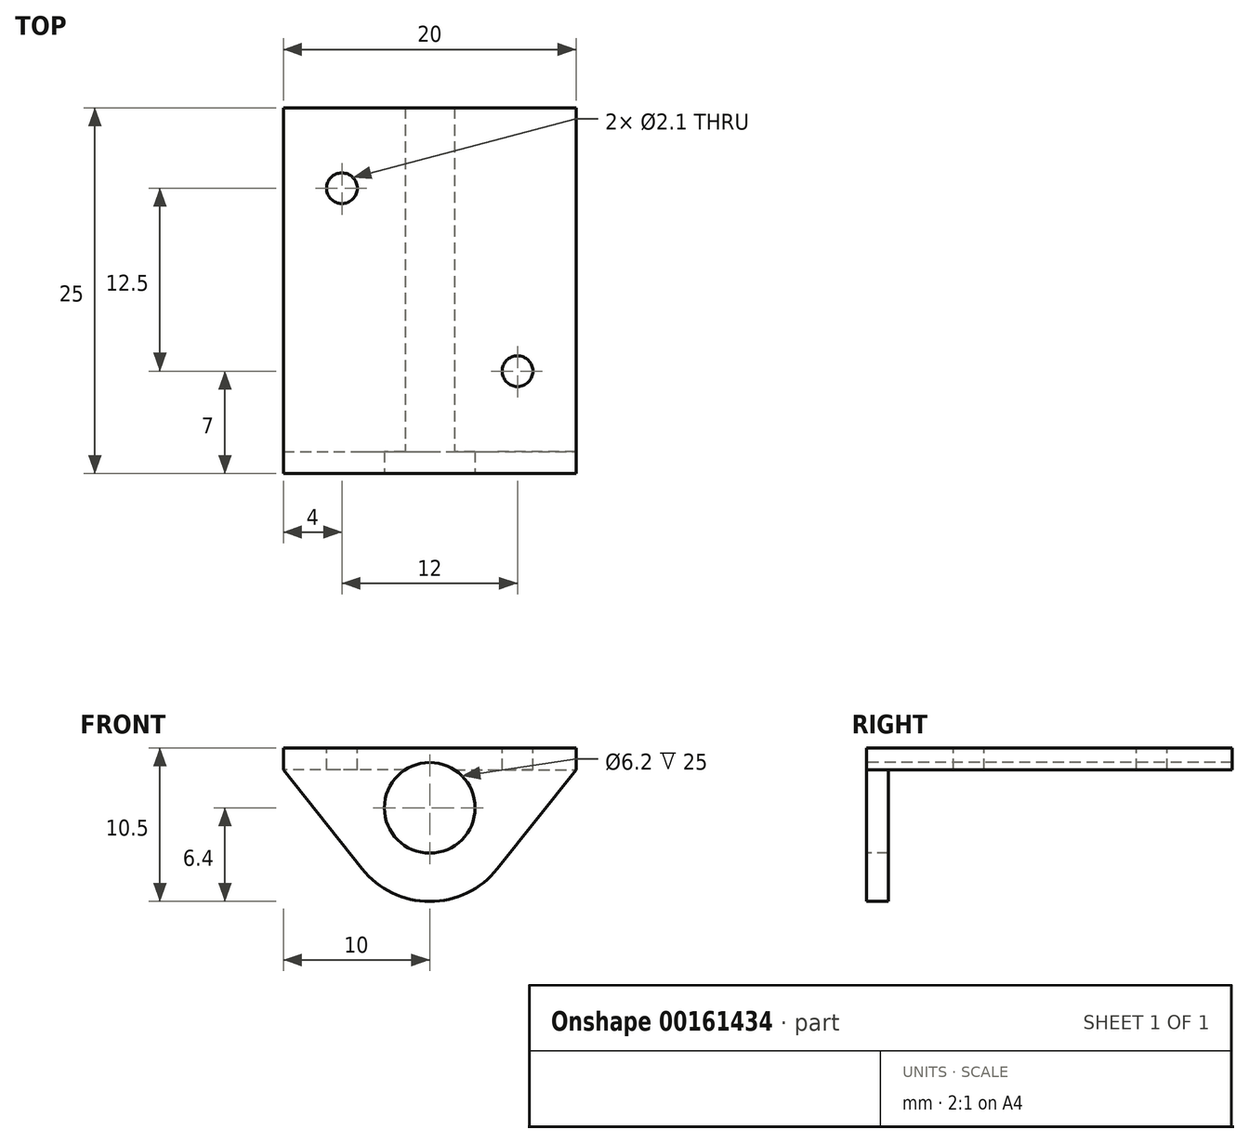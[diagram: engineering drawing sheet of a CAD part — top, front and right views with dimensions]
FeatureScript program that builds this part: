
annotation { "Feature Type Name" : "Feature", "Feature Type Description" : "" }
export const myFeature = defineFeature(function(context is Context, id is Id, definition is map)
    precondition{}
    {
        {
            var Q0;
            Q0=qCreatedBy(makeId("Top.planeOp"),FACE);
            var sketch = newSketch(context, id + "F0", { "sketchPlane" : qUnion([Q0])});
            skLineSegment(sketch, "E0.bottom", {"start": v(10, 12.5) * mm, "end": v(-10, 12.5) * mm});
            skLineSegment(sketch, "E0.top", {"start": v(10, -12.5) * mm, "end": v(-10, -12.5) * mm});
            skLineSegment(sketch, "E0.left", {"start": v(10, 12.5) * mm, "end": v(10, -12.5) * mm});
            skLineSegment(sketch, "E0.right", {"start": v(-10, 12.5) * mm, "end": v(-10, -12.5) * mm});
            skPoint(sketch, "E0.middle", {"position": v(0, 0) * mm});
            skCircle(sketch, "E1", {"center": v(6, -5.5) * mm, "radius": 1.05 * mm});
            skCircle(sketch, "E2", {"center": v(-6, 7) * mm, "radius": 1.05 * mm});
            skSolve(sketch);
        }
        {
            var Q0;
            Q0=makeQuery(id+"F0.imprint","IMPRINT",FACE,{"disambiguationData":[TD([[makeQuery(id+"F0.imprint","IMPRINT",EDGE,{"derivedFrom":sQuery(id+"F0.wireOp",EDGE,"E0.bottom")}),1.0]])]});
            extrude(context, id + "F1", {"entities" : qUnion([Q0]), "oppositeDirection" : true, "depth" : 1.5 * mm});
        }
        {
            var Q0;
            Q0=makeQuery(id+"F1.opExtrude","CAP_FACE",FACE,{"disambiguationData":[OSD([sQuery(id+"F0.wireOp",EDGE,"E0.bottom"),sQuery(id+"F0.wireOp",EDGE,"E0.top"),sQuery(id+"F0.wireOp",EDGE,"E0.left"),sQuery(id+"F0.wireOp",EDGE,"E0.right")])],"isStart":false});
            var sketch = newSketch(context, id + "F2", { "sketchPlane" : qUnion([Q0])});
            skLineSegment(sketch, "E3.bottom", {"start": v(-10, 12.5) * mm, "end": v(10, 12.5) * mm});
            skLineSegment(sketch, "E3.top", {"start": v(-10, 11) * mm, "end": v(10, 11) * mm});
            skLineSegment(sketch, "E3.left", {"start": v(-10, 12.5) * mm, "end": v(-10, 11) * mm});
            skLineSegment(sketch, "E3.right", {"start": v(10, 12.5) * mm, "end": v(10, 11) * mm});
            skSolve(sketch);
        }
        {
            var Q0;
            Q0 = qSketchRegion(id + "F2", true);
            extrude(context, id + "F3", {"entities" : qUnion([Q0]), "operationType" : NewBodyOperationType.ADD, "depth" : 9 * mm});
        }
        {
            var Q0;
            Q0=makeQuery(id+"F3.boolean.opBoolean","MERGE",FACE,{"derivedFrom":[makeQuery(id+"F1.opExtrude","SWEPT_FACE",FACE,{"disambiguationData":[OSD([sQuery(id+"F0.wireOp",EDGE,"E0.top")])]}),makeQuery(id+"F3.opExtrude","SWEPT_FACE",FACE,{"disambiguationData":[OSD([sQuery(id+"F2.wireOp",EDGE,"E3.bottom")])]})]});
            var sketch = newSketch(context, id + "F4", { "sketchPlane" : qUnion([Q0])});
            skCircle(sketch, "E4", {"center": v(0, -4.1) * mm, "radius": 3.1 * mm});
            skLineSegment(sketch, "E5", {"start": v(-10, -1.5) * mm, "end": v(-4.62, -8.27) * mm});
            skLineSegment(sketch, "E6", {"start": v(10, -1.5) * mm, "end": v(4.62, -8.27) * mm});
            skArc(sketch, "E7.trimOffspring", {"start": v(-4.62, -8.27) * mm, "mid": v(0, -10.5) * mm, "end": v(4.62, -8.27) * mm});
            skSolve(sketch);
        }
        {
            var Q0;
            Q0 = qSketchRegion(id + "F4", true);
            var Q1;
            {var subQ0=sQuery(id+"F4.wireOp",EDGE,"E5");Q1=makeQuery(id+"F4.imprint","IMPRINT",FACE,{"disambiguationData":[TD([[makeQuery(id+"F4.imprint","IMPRINT",EDGE,{"derivedFrom":subQ0}),-1.0]])]});}
            var Q2;
            {var subQ0=sQuery(id+"F4.wireOp",EDGE,"E6");Q2=makeQuery(id+"F4.imprint","IMPRINT",FACE,{"disambiguationData":[TD([[makeQuery(id+"F4.imprint","IMPRINT",EDGE,{"derivedFrom":subQ0}),1.0]])]});}
            extrude(context, id + "F5", {"entities" : qUnion([Q0, Q1, Q2]), "operationType" : NewBodyOperationType.REMOVE, "oppositeDirection" : true, "depth" : 30 * mm});
        }
    });
